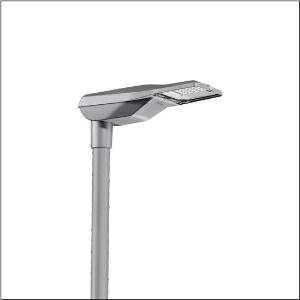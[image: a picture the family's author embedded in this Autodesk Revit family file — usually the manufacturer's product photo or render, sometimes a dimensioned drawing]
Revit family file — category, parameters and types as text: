
# Revit family: streetlight_sl_21_iq_micro___p0_5a_5xe1v31d08db_e47d
name_source: partatom
category: Lighting Fixtures
units: mm (PartAtom-declared; Revit-internal decimal feet)

## family parameters
Cut with Voids When Loaded = No
Host = Face
Light Source = No
Part Type = Normal
Room Calculation Point = No
Round Connector Dimension = Use Diameter
Shared = No

## types (1)
- --- (1 x LED, 4660 lm, 36.4 W, 3000K)
    Apparent Load = 36 VA
    CIE Flux Codes = 37 73 96 100 100
    Color Rendering = 70
    Color Temperature = 3000K
    Default Elevation = 1800 mm
    Description = Streetlight SL 21 iQ micro, mast luminaire, primary light control with lens, of PMMA, primary optical cover: cover, of toughened safety glass, transparent, light distribution: P0.5a, light emission: direct distribution, primary light characteristic: asymmetric, installation type: post-top, side-entry, LED, High Power LED, rated luminous flux: 4.660lm, luminous efficacy: 128lm/W, light colour: 730, colour temperature: 3000K, control gear: iQ-Comfort, control: pre-setting: linear dimming characteristic, Auto-Match, Temp-Guard, Lumen-Switch, Night-Set, Smart-Wire, Light-Fading, Desk-Remote (wireless, voltage-free reading and setting of iQ features in the workshop via application-optimized NFC function/RFID function), optimised constant luminous flux control (CLO 2.0), mains connection: 220..240V, AC, 50/60Hz, start of lifetime: 36W, end of service life: 38W, reduction: 16W, luminaire housing, of diecast aluminium, powder-coated, SITECO metallic grey (DB 702S), corrosivity category C5 high according to DIN EN ISO 12944, please order mast flange separately, inclination adjustable: 0°, 5°, 10°, 15°, sealing non-destructively replaceable, multi-level sealing system, length: 528mm, width: 235mm, height: 110mm, mast flange for spigot size: 42mm (side-entry): 5XC10008XM4, 60/48mm (side-entry/post-top): 5XC10108XM2, 76/60mm (side-entry/post-top): 5XC10108XM1, protection rating (complete): IP66, insulation class (complete): insulation class II (safety insulation), certification: CE, ENEC, ENEC+, VDE, impact resistance: IK10, permissible operating ambient temperature for outdoor applications: -40..+50°C, standard-compliant lighting for roads and squares, packaging unit: 1 piece

Light Distribution: P0.5a
    Height = 110 mm
    Lamp = 1 x LED
    Lamp Light Flux = 4660 lm
    Lamp Power = 36.4 W
    Lamp count = 1
    Length = 528 mm
    Luminous efficacy = 128 lm/W
    Manufacturer = Siteco
    ModVariant = No
    Model = 5XE1V31D08DB
    Mounting Place = Pole
    Mounting Type = Pole top
    Number of Poles = 1
    OnlyDefault = Yes
    Power Factor = 1
    Product Name = Streetlight SL 21 iQ micro | P0.5a
    Product group = mast luminaire | pylon top
    ProductGroupID = 6100
    Protection Class = Protection class II
    Protection Degree = IP 66
    RLX_Detail_Level = 1
    RLX_Emergency_Light_Flux = 0 lm
    RLX_Emergency_Type = 0
    RLX_Emergency_Type_DB = No
    RlxData = <blob elided: 98461 chars, md5=7cd28fe1>
    Socket = socket
    Standby Power = 0 W
    System Light Flux = 4660 lm
    System Power = 36 W
    Type Comments = factory setting: luminous flux: 100 % | dim-lin: 254 | 715 mA
    Type Image = l_1006881.jpg
    URL = http://relux.com
    VarID = @adj_079707
    Voltage = 0 V
    Weight = 0.00 kg
    Width = 235 mm

## geometry (parser evidence)
native form markers: Blend x4, Sweep x9
no freeform markers — native parametric forms only
